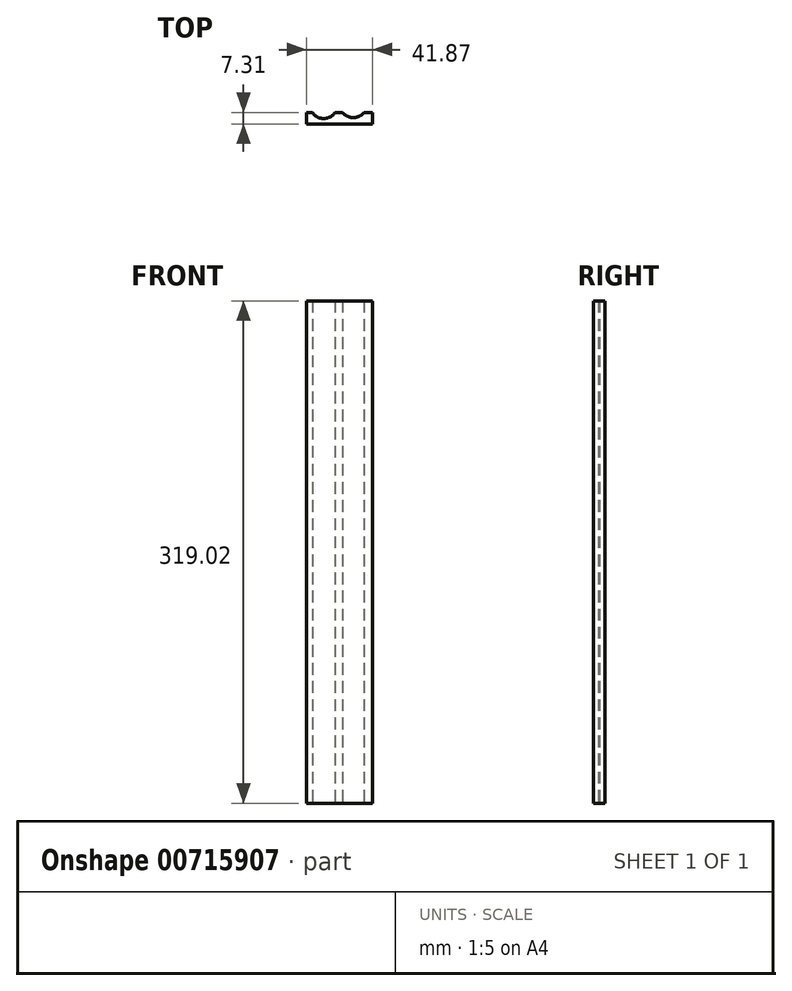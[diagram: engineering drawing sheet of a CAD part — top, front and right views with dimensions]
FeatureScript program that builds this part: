
annotation { "Feature Type Name" : "Feature", "Feature Type Description" : "" }
export const myFeature = defineFeature(function(context is Context, id is Id, definition is map)
    precondition{}
    {
        {
            var Q0;
            Q0=qCreatedBy(makeId("Top.planeOp"),FACE);
            var sketch = newSketch(context, id + "F0", { "sketchPlane" : qUnion([Q0])});
            skLineSegment(sketch, "E0", {"start": v(0, 0) * mm, "end": v(38.15, 0) * mm});
            skLineSegment(sketch, "E1", {"start": v(38.15, 0) * mm, "end": v(38.15, 7.31) * mm});
            skLineSegment(sketch, "E2", {"start": v(38.15, 7.31) * mm, "end": v(32.87, 7.31) * mm});
            skArc(sketch, "E3", {"start": v(19.08, 7.31) * mm, "mid": v(25.97, 3.96) * mm, "end": v(32.87, 7.31) * mm});
            skPoint(sketch, "E3.startSnap0", {"position": v(19.08, 0) * mm});
            skLineSegment(sketch, "E4", {"start": v(19.08, 7.31) * mm, "end": v(14.36, 7.31) * mm});
            skArc(sketch, "E5", {"start": v(0, 7.31) * mm, "mid": v(7.18, 3.35) * mm, "end": v(14.36, 7.31) * mm});
            skLineSegment(sketch, "E6", {"start": v(0, 7.31) * mm, "end": v(-3.72, 7.31) * mm});
            skLineSegment(sketch, "E7", {"start": v(-3.72, 7.31) * mm, "end": v(-3.72, 0) * mm});
            skLineSegment(sketch, "E8", {"start": v(-3.72, 0) * mm, "end": v(0, 0) * mm});
            skSolve(sketch);
        }
        {
            var Q0;
            Q0=makeQuery(id+"F0.imprint","IMPRINT",FACE,{"disambiguationData":[TD([[makeQuery(id+"F0.imprint","IMPRINT",EDGE,{"derivedFrom":sQuery(id+"F0.wireOp",EDGE,"E0")}),1.0]])]});
            extrude(context, id + "F1", {"entities" : qUnion([Q0]), "depth" : 319.02 * mm, "offsetDistance" : 25.4 * mm});
        }
    });
